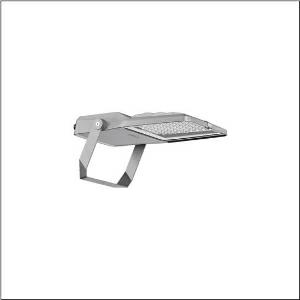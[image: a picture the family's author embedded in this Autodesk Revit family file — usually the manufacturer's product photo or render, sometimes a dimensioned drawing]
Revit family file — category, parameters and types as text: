
# Revit family: floodlight_fl_21_mini___pl43_5xa7775d2a1a_a4ba
name_source: partatom
category: Lighting Fixtures
units: mm (PartAtom-declared; Revit-internal decimal feet)

## family parameters
Cut with Voids When Loaded = No
Host = Face
Light Source = No
Part Type = Normal
Room Calculation Point = No
Round Connector Dimension = Use Diameter
Shared = No

## types (1)
- --- (1 x LED, 18300 lm, 142.9 W, 3000K)
    Apparent Load = 143 VA
    CIE Flux Codes = 27 78 99 100 100
    Color Rendering = 70
    Color Temperature = 3000K
    Default Elevation = 1800 mm
    Description = Floodlight FL 21 mini, floodlight, primary light control with lens, of PMMA, primary optical cover: protective disc, of toughened safety glass, transparent, light distribution: PL43, light emission: direct distribution, installation type: surface-mounted, LED, High Power LED, rated luminous flux: 18.300lm, luminous efficacy: 128lm/W, light colour: 730, colour temperature: 3000K, control gear: Smart Interface (Zhaga), control: flexible luminous flux parameterisation, time-dependent luminous flux control, constant luminous flux control, overheat protection, pre-setting: logarithmic dimming characteristic, with terminal, 6-pole, mains connection: 220..240V, AC, 50/60Hz, start of lifetime: 143W, end of service life: 151W, reduction: 63W, luminaire housing, of diecast aluminium, powder-coated, Siteco® metallic grey (DB 702S), corrosivity category C5 mid according to DIN EN ISO 12944, suitable for swimming pools, chlorine-resistant, sealing non-destructively replaceable, mounting bracket, of steel, galvanised, powder-coated, Siteco® metallic grey (DB 702S), Smart Interface above, protection rating (complete): IP66, insulation class (complete): insulation class II (safety insulation), certification: CE, ENEC, VDE, protection symbol: D, impact resistance: IK08, permissible operating ambient temperature: -40..+40°C, permissible operating ambient temperature for outdoor applications: -40..+50°C, standard: DIN EN 12944, LABS conformity tested according to VDMA 24364:2018-05, packaging unit: 1 piece

Light Distribution: PL43
    Height = 70 mm
    Lamp = 1 x LED
    Lamp Light Flux = 18300 lm
    Lamp Power = 142.9 W
    Lamp count = 1
    Length = 485 mm
    Luminous efficacy = 128 lm/W
    Manufacturer = Siteco
    ModVariant = No
    Model = 5XA7775D2A1A
    Number of Poles = 1
    OnlyDefault = Yes
    Power Factor = 1
    Product Name = Floodlight FL 21 mini | PL43
    Product group = floodlight | pylon annexe
    ProductGroupID = 6200
    Protection Class = Protection class II
    Protection Degree = IP 66
    RLX_Detail_Level = 1
    RLX_Emergency_Light_Flux = 0 lm
    RLX_Emergency_Type = 0
    RLX_Emergency_Type_DB = No
    RlxData = <blob elided: 96217 chars, md5=ffef4835>
    Socket = socket
    Standby Power = 0 W
    System Light Flux = 18300 lm
    System Power = 143 W
    Type Comments = factory setting: luminous flux: 100 % | dim-lin: 254 | 730 mA
    Type Image = l_1006845.jpg
    URL = http://relux.com
    VarID = @adj_161060
    Voltage = 0 V
    Weight = 0.00 kg
    Width = 337 mm

## geometry (parser evidence)
native form markers: Blend x4, Sweep x10
no freeform markers — native parametric forms only
